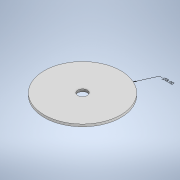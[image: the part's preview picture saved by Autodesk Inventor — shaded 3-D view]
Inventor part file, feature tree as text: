
AUTODESK INVENTOR PART (.ipt)
format: ipt  version: 2021 (Build 250183000, 183)  size: 105,984 bytes
history: native  units: in
note: dims shown in document units (in); Inventor stores cm internally (conversion verified against a paired STEP export)
features: other x2, extrude x2, sketch x2
ambient origin geometry x8: Origin, YZ Plane, XZ Plane, XY Plane, X Axis, Y Axis, Z Axis, Center Point
bodies: Solid1 (feature_tree)
feature tree (6):
  other  "Annotations"
  extrude  "Extrusion1"  Depth=0.25in TaperAngle=0.0deg
  extrude  "Extrusion2"  TaperAngle=0.0deg  [1 undecoded]
  sketch  "Sketch1"  dims[d0=8.0in d1=0.25in d2=0.0in]
  sketch  "Sketch2"  dims[d5=1.0in d6=0.0in d7=0.0in d3=1.6868in d4=8.0in]
  other  "Diameter Dimension 1"
note: 1 required parameter value undecoded (feature->parameter linkage not recoverable at this tier; creation-order binding heuristic only, values carry confidence <= 0.55)
